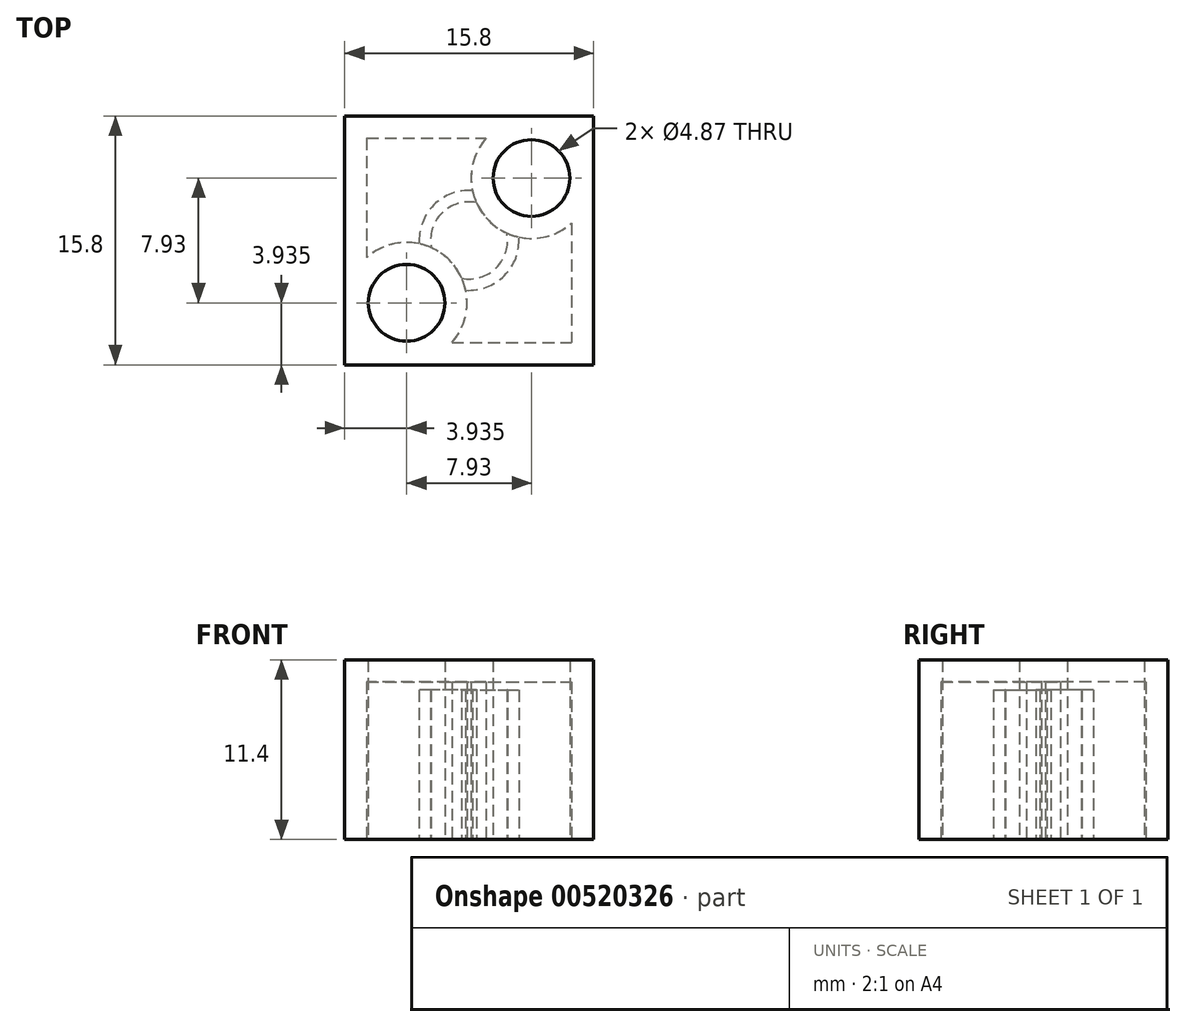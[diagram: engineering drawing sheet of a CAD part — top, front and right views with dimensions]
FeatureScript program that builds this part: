
annotation { "Feature Type Name" : "Feature", "Feature Type Description" : "" }
export const myFeature = defineFeature(function(context is Context, id is Id, definition is map)
    precondition{}
    {
        {
            var Q0;
            Q0=qCreatedBy(makeId("Top.planeOp"),FACE);
            var sketch = newSketch(context, id + "F0", { "sketchPlane" : qUnion([Q0])});
            skLineSegment(sketch, "E0.bottom", {"start": v(-7.9, 7.9) * mm, "end": v(7.9, 7.9) * mm});
            skLineSegment(sketch, "E0.top", {"start": v(-7.9, -7.9) * mm, "end": v(7.9, -7.9) * mm});
            skLineSegment(sketch, "E0.left", {"start": v(-7.9, 7.9) * mm, "end": v(-7.9, -7.9) * mm});
            skLineSegment(sketch, "E0.right", {"start": v(7.9, 7.9) * mm, "end": v(7.9, -7.9) * mm});
            skPoint(sketch, "E0.middle", {"position": v(0, 0) * mm});
            skPoint(sketch, "E1.endSnap0", {"position": v(0, 7.9) * mm});
            skCircle(sketch, "E2", {"center": v(-3.96, 3.97) * mm, "radius": 2.44 * mm});
            skCircle(sketch, "E3.MirrorC", {"center": v(3.96, 3.97) * mm, "radius": 2.44 * mm});
            skCircle(sketch, "E4.MirrorC", {"center": v(-3.96, -3.97) * mm, "radius": 2.44 * mm});
            skCircle(sketch, "E5.MirrorC", {"center": v(3.96, -3.97) * mm, "radius": 2.44 * mm});
            skLineSegment(sketch, "E6", {"start": v(-6.4, 3.97) * mm, "end": v(-7.9, 3.97) * mm});
            skLineSegment(sketch, "E7", {"start": v(-1.53, 3.97) * mm, "end": v(1.53, 3.97) * mm});
            skSolve(sketch);
        }
        {
            var Q0;
            Q0=makeQuery(id+"F0.imprint","IMPRINT",FACE,{"disambiguationData":[TD([[makeQuery(id+"F0.imprint","IMPRINT",EDGE,{"derivedFrom":sQuery(id+"F0.wireOp",EDGE,"E0.bottom")}),-1.0]])]});
            extrude(context, id + "F1", {"entities" : qUnion([Q0]), "depth" : 9.6 * mm, "offsetDistance" : 25 * mm});
        }
        {
            var Q0;
            Q0=makeQuery(id+"F0.imprint","IMPRINT",FACE,{"disambiguationData":[TD([[makeQuery(id+"F0.imprint","IMPRINT",EDGE,{"derivedFrom":sQuery(id+"F0.wireOp",EDGE,"E2")}),1.0]])]});
            var Q1;
            Q1=makeQuery(id+"F0.imprint","IMPRINT",FACE,{"disambiguationData":[TD([[makeQuery(id+"F0.imprint","IMPRINT",EDGE,{"derivedFrom":sQuery(id+"F0.wireOp",EDGE,"E3.MirrorC")}),-1.0]])]});
            var Q2;
            Q2=makeQuery(id+"F0.imprint","IMPRINT",FACE,{"disambiguationData":[TD([[makeQuery(id+"F0.imprint","IMPRINT",EDGE,{"derivedFrom":sQuery(id+"F0.wireOp",EDGE,"E5.MirrorC")}),1.0]])]});
            var Q3;
            Q3=makeQuery(id+"F0.imprint","IMPRINT",FACE,{"disambiguationData":[TD([[makeQuery(id+"F0.imprint","IMPRINT",EDGE,{"derivedFrom":sQuery(id+"F0.wireOp",EDGE,"E4.MirrorC")}),-1.0]])]});
            extrude(context, id + "F2", {"entities" : qUnion([Q0, Q1, Q2, Q3]), "operationType" : NewBodyOperationType.ADD, "depth" : 11.4 * mm, "offsetDistance" : 25 * mm});
        }
        {
            var Q0;
            {var subQ0=sQuery(id+"F0.wireOp",EDGE,"E5.MirrorC");var subQ1=sQuery(id+"F0.wireOp",EDGE,"E4.MirrorC");var subQ2=sQuery(id+"F0.wireOp",EDGE,"E3.MirrorC");var subQ3=sQuery(id+"F0.wireOp",EDGE,"E2");Q0=makeQuery(id+"F2.boolean.opBoolean","MERGE",FACE,{"derivedFrom":[makeQuery(id+"F1.opExtrude","CAP_FACE",FACE,{"disambiguationData":[OSD([sQuery(id+"F0.wireOp",EDGE,"E0.bottom"),sQuery(id+"F0.wireOp",EDGE,"E0.top"),sQuery(id+"F0.wireOp",EDGE,"E0.left"),sQuery(id+"F0.wireOp",EDGE,"E0.right"),subQ3,subQ2,subQ1,subQ0])],"isStart":true}),makeQuery(id+"F2.opExtrude","CAP_FACE",FACE,{"disambiguationData":[OSD([subQ3])],"isStart":true}),makeQuery(id+"F2.opExtrude","CAP_FACE",FACE,{"disambiguationData":[OSD([subQ2])],"isStart":true}),makeQuery(id+"F2.opExtrude","CAP_FACE",FACE,{"disambiguationData":[OSD([subQ1])],"isStart":true}),makeQuery(id+"F2.opExtrude","CAP_FACE",FACE,{"disambiguationData":[OSD([subQ0])],"isStart":true})]});}
            shell(context, id + "F3", {"entities" : qUnion([Q0]), "thickness" : 1.4 * mm});
        }
        {
            var Q0;
            {var subQ3=sQuery(id+"F0.wireOp",EDGE,"E0.bottom");Q0=makeQuery(id+"F0.imprint","IMPRINT",FACE,{"disambiguationData":[TD([[makeQuery(id+"F0.imprint","IMPRINT",EDGE,{"derivedFrom":subQ3}),-1.0]])]});}
            var sketch = newSketch(context, id + "F4", { "sketchPlane" : qUnion([Q0])});
            skCircle(sketch, "E8", {"center": v(0, 0) * mm, "radius": 3.17 * mm});
            skCircle(sketch, "E9", {"center": v(0, 0) * mm, "radius": 2.44 * mm});
            skSolve(sketch);
        }
        {
            var Q0;
            Q0=makeQuery(id+"F4.imprint","IMPRINT",FACE,{"disambiguationData":[TD([[makeQuery(id+"F4.imprint","IMPRINT",EDGE,{"derivedFrom":sQuery(id+"F4.wireOp",EDGE,"E8")}),1.0]])]});
            extrude(context, id + "F5", {"entities" : qUnion([Q0]), "operationType" : NewBodyOperationType.ADD, "depth" : 9.5 * mm, "offsetDistance" : 25 * mm});
        }
    });
